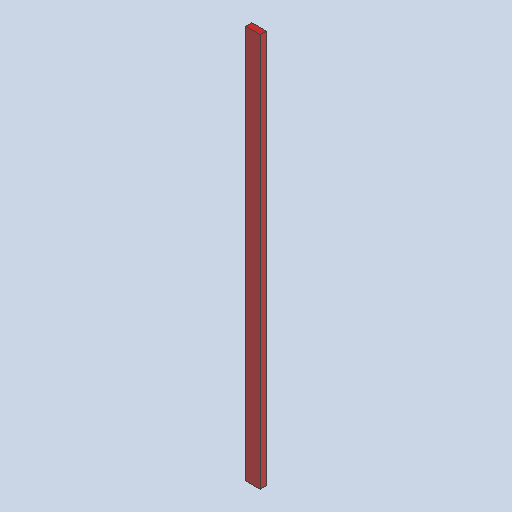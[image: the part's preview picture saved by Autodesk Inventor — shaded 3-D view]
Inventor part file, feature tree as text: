
AUTODESK INVENTOR PART (.ipt)
format: ipt  version: 2025.1 (Build 291241020, 241B)  size: 257,024 bytes
history: native  units: in
note: dims shown in document units (in); Inventor stores cm internally (conversion verified against a paired STEP export)
features: extrude x1, sketch x1, other x1
ambient origin geometry x8: Origin, YZ Plane, XZ Plane, XY Plane, X Axis, Y Axis, Z Axis, Center Point
bodies: Solid1 (feature_tree)
feature tree (3):
  extrude  "Extrusion1"  Depth=3.5in
  sketch  "Sketch1"  dims[d0=1.5in d1=3.5in d2=96.0in d3=0.0in]
  other  "Finish1"
